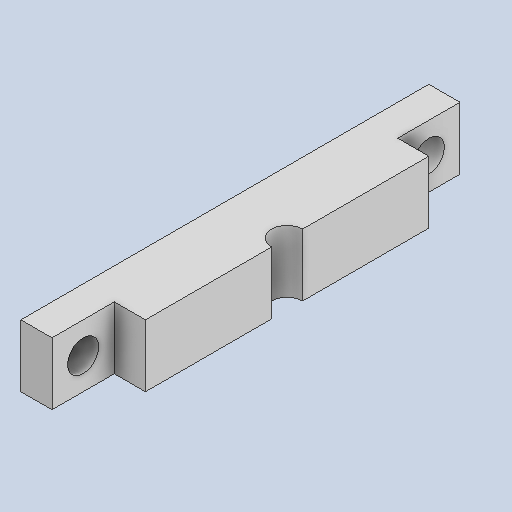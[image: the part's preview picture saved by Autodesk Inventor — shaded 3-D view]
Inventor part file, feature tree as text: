
AUTODESK INVENTOR PART (.ipt)
format: ipt  version: 2023 (Build 270158000, 158)  size: 134,144 bytes
history: native  units: mm
features: extrude x3, sketch x2
ambient origin geometry x8: Origin, YZ Plane, XZ Plane, XY Plane, X Axis, Y Axis, Z Axis, Center Point
bodies: Solid1 (feature_tree)
feature tree (5):
  sketch  "Sketch1"  dims[d0=10.0mm d1=0.0mm d2=5.0mm d3=0.0mm]
  extrude  "Extrusion1"  Depth=5.0mm TaperAngle=0.0deg
  extrude  "Extrusion2"  Depth=10.0mm TaperAngle=0.0deg
  extrude  "Extrusion4"  [1 undecoded]
  sketch  "Sketch4"  dims[d7=5.0mm d8=10.0mm d9=0.0mm]
note: 1 required parameter value undecoded (feature->parameter linkage not recoverable at this tier; creation-order binding heuristic only, values carry confidence <= 0.55)
